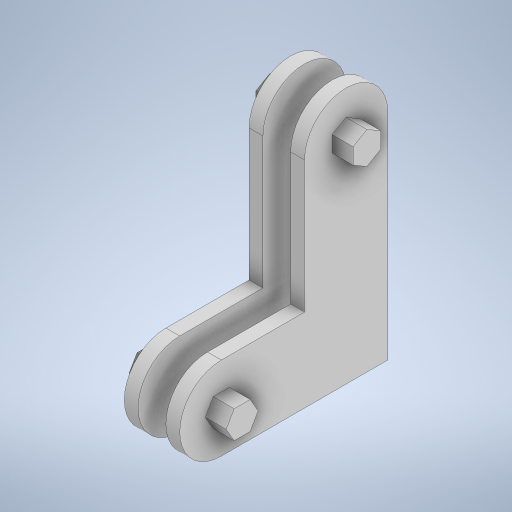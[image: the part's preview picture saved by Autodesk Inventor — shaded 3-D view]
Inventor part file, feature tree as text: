
AUTODESK INVENTOR PART (.ipt)
format: ipt  version: 2023 (Build 270158000, 158)  size: 299,520 bytes
history: native  units: in
note: dims shown in document units (in); Inventor stores cm internally (conversion verified against a paired STEP export)
features: extrude x2, sketch x2, plane x1, mirror x1
ambient origin geometry x8: Origin, YZ Plane, XZ Plane, XY Plane, X Axis, Y Axis, Z Axis, Center Point
bodies: Solid1 (feature_tree)
feature tree (6):
  extrude  "Extrusion1"  Depth=3.0in
  plane  "Work Plane1"
  extrude  "Extrusion2"  TaperAngle=0.0deg  [1 undecoded]
  mirror  "Mirror2"
  sketch  "Sketch1"  dims[d1=3.0in d2=3.0in]
  sketch  "Sketch2"  dims[d5=0.5in d6=0.0in d7=0.0in d8=4.75in d9=0.0in d10=3.0in d11=1.0in d12=1.0in d13=1.0in d14=0.75in d15=0.0in]
note: 1 required parameter value undecoded (feature->parameter linkage not recoverable at this tier; creation-order binding heuristic only, values carry confidence <= 0.55)
